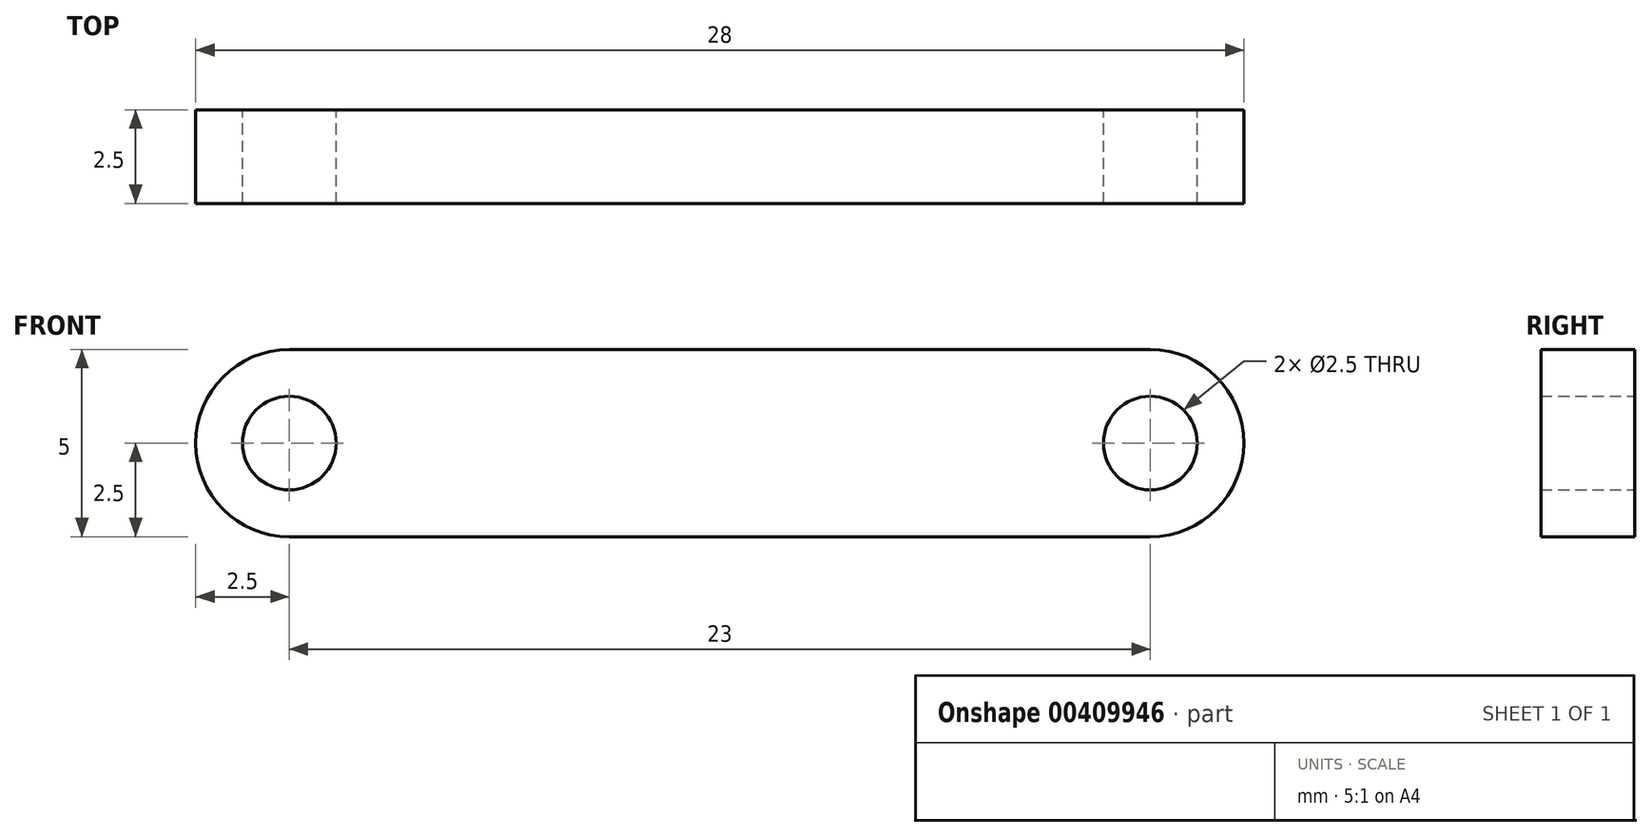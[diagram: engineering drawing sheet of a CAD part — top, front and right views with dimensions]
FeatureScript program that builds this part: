
annotation { "Feature Type Name" : "Feature", "Feature Type Description" : "" }
export const myFeature = defineFeature(function(context is Context, id is Id, definition is map)
    precondition{}
    {
        {
            var Q0;
            Q0=qCreatedBy(makeId("Front.planeOp"),FACE);
            var sketch = newSketch(context, id + "F0", { "sketchPlane" : qUnion([Q0])});
            skCircle(sketch, "E0", {"center": v(-23, 0) * mm, "radius": 1.25 * mm});
            skCircle(sketch, "E1", {"center": v(0, 0) * mm, "radius": 1.25 * mm});
            skArc(sketch, "E2", {"start": v(-23, 2.5) * mm, "mid": v(-25.5, 0) * mm, "end": v(-23, -2.5) * mm});
            skArc(sketch, "E3", {"start": v(0, -2.5) * mm, "mid": v(2.5, 0) * mm, "end": v(0, 2.5) * mm});
            skLineSegment(sketch, "E4", {"start": v(-23, 2.5) * mm, "end": v(0, 2.5) * mm});
            skLineSegment(sketch, "E5", {"start": v(-23, -2.5) * mm, "end": v(0, -2.5) * mm});
            skSolve(sketch);
        }
        {
            var Q0;
            Q0=makeQuery(id+"F0.imprint","IMPRINT",FACE,{"disambiguationData":[TD([[makeQuery(id+"F0.imprint","IMPRINT",EDGE,{"derivedFrom":sQuery(id+"F0.wireOp",EDGE,"E0")}),-1.0]])]});
            extrude(context, id + "F1", {"entities" : qUnion([Q0]), "depth" : 2.5 * mm});
        }
    });
